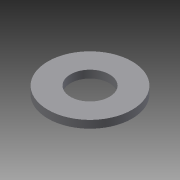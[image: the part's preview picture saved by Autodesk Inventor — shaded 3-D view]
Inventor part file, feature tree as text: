
AUTODESK INVENTOR PART (.ipt)
format: ipt  version: 2013 (Build 170138000, 138)  size: 71,680 bytes
history: native  units: mm
features: extrude x1, sketch x1
ambient origin geometry x8: Origin, YZ Plane, XZ Plane, XY Plane, X Axis, Y Axis, Z Axis, Center Point
bodies: Solid1 (feature_tree)
feature tree (2):
  extrude  "Extrusion1"  Depth=5.1mm
  sketch  "Sketch1"  dims[d0=11.0mm d2=5.1mm d3=1.0mm d4=0.0mm]
